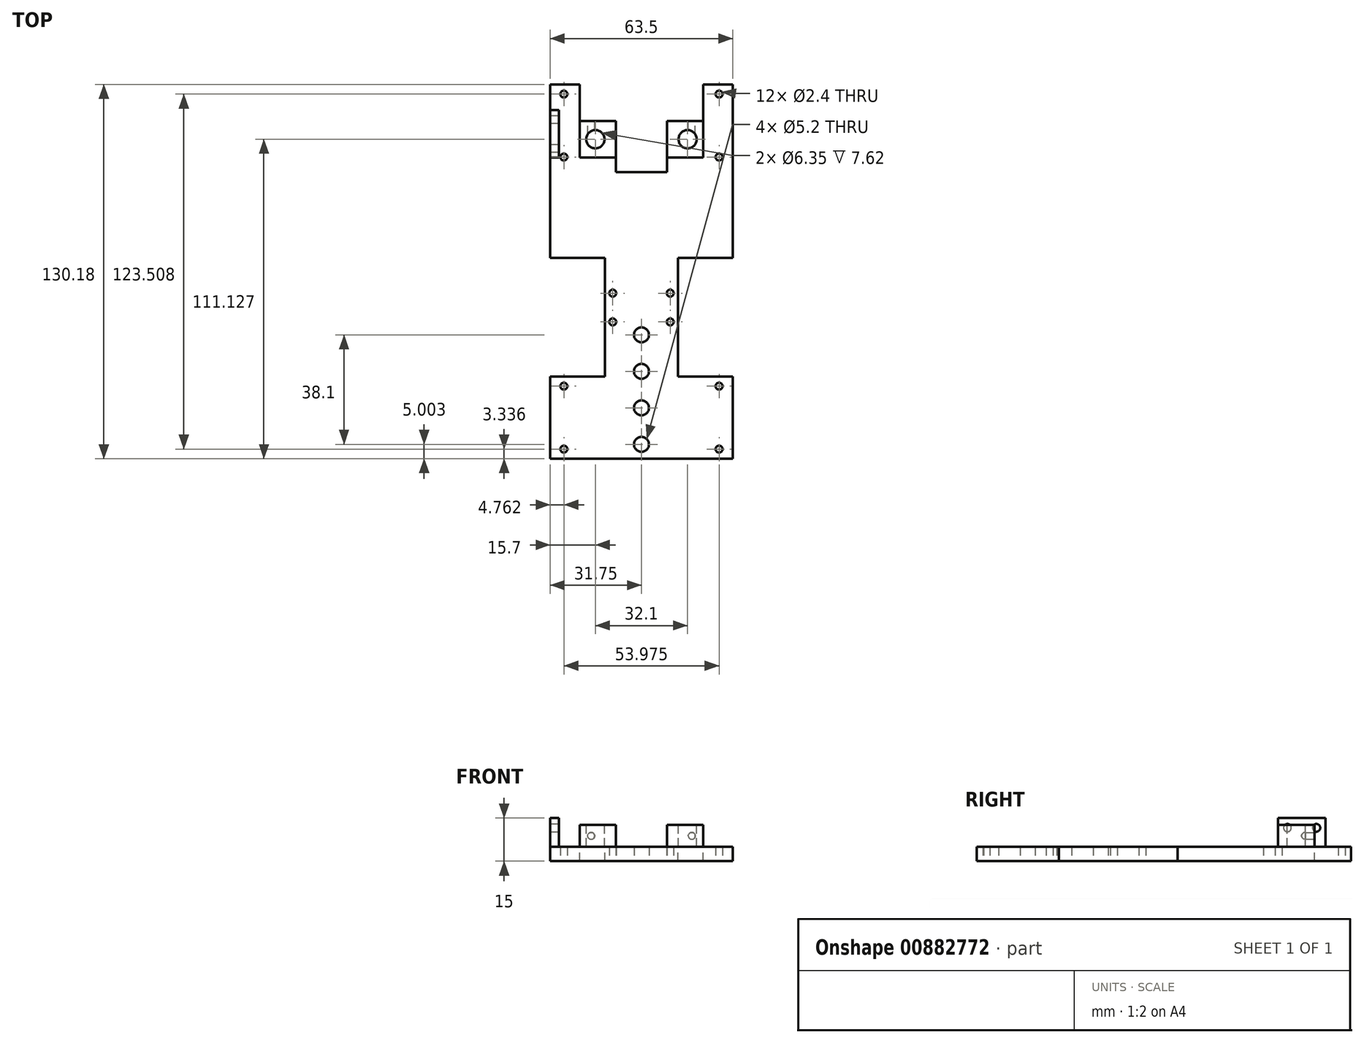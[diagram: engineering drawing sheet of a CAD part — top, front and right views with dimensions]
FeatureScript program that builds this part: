
annotation { "Feature Type Name" : "Feature", "Feature Type Description" : "" }
export const myFeature = defineFeature(function(context is Context, id is Id, definition is map)
    precondition{}
    {
        {
            var Q0;
            Q0=qCreatedBy(makeId("Top.planeOp"),FACE);
            var sketch = newSketch(context, id + "F0", { "sketchPlane" : qUnion([Q0])});
            skLineSegment(sketch, "E0.left", {"start": v(-12.7, 36.51) * mm, "end": v(-12.7, -36.51) * mm});
            skLineSegment(sketch, "E0.right", {"start": v(12.7, 36.51) * mm, "end": v(12.7, -36.51) * mm});
            skPoint(sketch, "E0.middle", {"position": v(0, 0) * mm});
            skLineSegment(sketch, "E1.bottom", {"start": v(-31.75, 65.09) * mm, "end": v(31.75, 65.09) * mm});
            skLineSegment(sketch, "E1.top", {"start": v(-31.75, 36.51) * mm, "end": v(-12.7, 36.51) * mm});
            skLineSegment(sketch, "E1.left", {"start": v(-31.75, 65.09) * mm, "end": v(-31.75, 36.51) * mm});
            skLineSegment(sketch, "E1.right", {"start": v(31.75, 65.09) * mm, "end": v(31.75, 36.51) * mm});
            skLineSegment(sketch, "E2.bottom", {"start": v(-31.75, -65.09) * mm, "end": v(31.75, -65.09) * mm});
            skLineSegment(sketch, "E2.top", {"start": v(-31.75, -36.51) * mm, "end": v(-12.7, -36.51) * mm});
            skLineSegment(sketch, "E2.left", {"start": v(-31.75, -65.09) * mm, "end": v(-31.75, -36.51) * mm});
            skLineSegment(sketch, "E2.right", {"start": v(31.75, -65.09) * mm, "end": v(31.75, -36.51) * mm});
            skLineSegment(sketch, "E3.trimOffspring", {"start": v(12.7, 36.51) * mm, "end": v(31.75, 36.51) * mm});
            skLineSegment(sketch, "E4.trimOffspring", {"start": v(12.7, -36.51) * mm, "end": v(31.75, -36.51) * mm});
            skLineSegment(sketch, "E5", {"start": v(0, -33.1) * mm, "end": v(0, -96.6) * mm});
            skLineSegment(sketch, "E6", {"start": v(-134.87, 0) * mm, "end": v(102.97, 0) * mm});
            skCircle(sketch, "E7", {"center": v(-26.99, 61.75) * mm, "radius": 1.2 * mm});
            skCircle(sketch, "E8", {"center": v(-26.99, 39.85) * mm, "radius": 1.2 * mm});
            skCircle(sketch, "E9", {"center": v(26.99, 61.75) * mm, "radius": 1.2 * mm});
            skCircle(sketch, "E10", {"center": v(26.99, 39.85) * mm, "radius": 1.2 * mm});
            skCircle(sketch, "E11", {"center": v(26.99, -39.85) * mm, "radius": 1.2 * mm});
            skCircle(sketch, "E12", {"center": v(26.99, -61.75) * mm, "radius": 1.2 * mm});
            skCircle(sketch, "E13", {"center": v(-26.99, -61.75) * mm, "radius": 1.2 * mm});
            skCircle(sketch, "E14", {"center": v(-26.99, -39.85) * mm, "radius": 1.2 * mm});
            skLineSegment(sketch, "E15", {"start": v(-31.75, 50.8) * mm, "end": v(31.75, 50.8) * mm});
            skLineSegment(sketch, "E16", {"start": v(-31.75, -50.8) * mm, "end": v(31.75, -50.8) * mm});
            skLineSegment(sketch, "E17.direction1", {"start": v(0, 60.09) * mm, "end": v(25.4, 60.09) * mm, "construction": true});
            skLineSegment(sketch, "E17.direction2", {"start": v(0, 60.09) * mm, "end": v(0, 47.39) * mm, "construction": true});
            skCircle(sketch, "E18", {"center": v(0, -60.09) * mm, "radius": 2.6 * mm});
            skCircle(sketch, "E19.0.1.0", {"center": v(0, -47.39) * mm, "radius": 2.6 * mm});
            skCircle(sketch, "E19.0.2.0", {"center": v(0, -34.69) * mm, "radius": 2.6 * mm});
            skCircle(sketch, "E19.0.3.0", {"center": v(0, -21.99) * mm, "radius": 2.6 * mm});
            skLineSegment(sketch, "E19.direction1", {"start": v(0, -60.09) * mm, "end": v(25.4, -60.09) * mm, "construction": true});
            skLineSegment(sketch, "E19.direction2", {"start": v(0, -60.09) * mm, "end": v(0, -47.39) * mm, "construction": true});
            skLineSegment(sketch, "E20", {"start": v(0, 65.09) * mm, "end": v(0, -50.8) * mm});
            skCircle(sketch, "E21", {"center": v(-10, -7.5) * mm, "radius": 1.2 * mm});
            skCircle(sketch, "E22", {"center": v(-10, -17.5) * mm, "radius": 1.2 * mm});
            skCircle(sketch, "E23.MirrorC", {"center": v(10, -7.5) * mm, "radius": 1.2 * mm});
            skCircle(sketch, "E24.MirrorC", {"center": v(10, -17.5) * mm, "radius": 1.2 * mm});
            skSolve(sketch);
        }
        {
            var Q0;
            Q0 = qSketchRegion(id + "F0", true);
            extrude(context, id + "F1", {"entities" : qUnion([Q0]), "depth" : 5 * mm, "offsetDistance" : 25.4 * mm});
        }
        {
            var Q0;
            Q0=makeQuery(id+"F1.opExtrude","CAP_FACE",FACE,{"disambiguationData":[OSD([sQuery(id+"F0.wireOp",EDGE,"E0.left"),sQuery(id+"F0.wireOp",EDGE,"E0.right"),sQuery(id+"F0.wireOp",EDGE,"E1.bottom"),sQuery(id+"F0.wireOp",EDGE,"E1.top"),sQuery(id+"F0.wireOp",EDGE,"E1.left"),sQuery(id+"F0.wireOp",EDGE,"E1.right"),sQuery(id+"F0.wireOp",EDGE,"E2.bottom"),sQuery(id+"F0.wireOp",EDGE,"E2.top"),sQuery(id+"F0.wireOp",EDGE,"E2.left"),sQuery(id+"F0.wireOp",EDGE,"E2.right"),sQuery(id+"F0.wireOp",EDGE,"E3.trimOffspring"),sQuery(id+"F0.wireOp",EDGE,"E4.trimOffspring"),sQuery(id+"F0.wireOp",EDGE,"E7"),sQuery(id+"F0.wireOp",EDGE,"E8"),sQuery(id+"F0.wireOp",EDGE,"E9"),sQuery(id+"F0.wireOp",EDGE,"E10"),sQuery(id+"F0.wireOp",EDGE,"E11"),sQuery(id+"F0.wireOp",EDGE,"E12"),sQuery(id+"F0.wireOp",EDGE,"E13"),sQuery(id+"F0.wireOp",EDGE,"E14"),sQuery(id+"F0.wireOp",EDGE,"E18"),sQuery(id+"F0.wireOp",EDGE,"E19.0.1.0"),sQuery(id+"F0.wireOp",EDGE,"E19.0.2.0"),sQuery(id+"F0.wireOp",EDGE,"E19.0.3.0"),sQuery(id+"F0.wireOp",EDGE,"E21"),sQuery(id+"F0.wireOp",EDGE,"E22"),sQuery(id+"F0.wireOp",EDGE,"E23.MirrorC"),sQuery(id+"F0.wireOp",EDGE,"E24.MirrorC")])],"isStart":false});
            var sketch = newSketch(context, id + "F2", { "sketchPlane" : qUnion([Q0])});
            skLineSegment(sketch, "E25.bottom", {"start": v(-31.75, 36.51) * mm, "end": v(-12.7, 36.51) * mm});
            skLineSegment(sketch, "E25.top", {"start": v(-31.75, 4.76) * mm, "end": v(-12.7, 4.76) * mm});
            skLineSegment(sketch, "E25.left", {"start": v(-31.75, 36.51) * mm, "end": v(-31.75, 4.76) * mm});
            skLineSegment(sketch, "E25.right", {"start": v(-12.7, 36.51) * mm, "end": v(-12.7, 4.76) * mm});
            skLineSegment(sketch, "E26.bottom", {"start": v(12.7, 36.51) * mm, "end": v(31.75, 36.51) * mm});
            skLineSegment(sketch, "E26.top", {"start": v(12.7, 4.76) * mm, "end": v(31.75, 4.76) * mm});
            skLineSegment(sketch, "E26.left", {"start": v(12.7, 36.51) * mm, "end": v(12.7, 4.76) * mm});
            skLineSegment(sketch, "E26.right", {"start": v(31.75, 36.51) * mm, "end": v(31.75, 4.76) * mm});
            skSolve(sketch);
        }
        {
            var Q0;
            Q0 = qSketchRegion(id + "F2", true);
            var Q1;
            Q1=makeQuery(id+"F1.opExtrude","CAP_FACE",FACE,{"disambiguationData":[OSD([sQuery(id+"F0.wireOp",EDGE,"E0.left"),sQuery(id+"F0.wireOp",EDGE,"E0.right"),sQuery(id+"F0.wireOp",EDGE,"E1.bottom"),sQuery(id+"F0.wireOp",EDGE,"E1.top"),sQuery(id+"F0.wireOp",EDGE,"E1.left"),sQuery(id+"F0.wireOp",EDGE,"E1.right"),sQuery(id+"F0.wireOp",EDGE,"E2.bottom"),sQuery(id+"F0.wireOp",EDGE,"E2.top"),sQuery(id+"F0.wireOp",EDGE,"E2.left"),sQuery(id+"F0.wireOp",EDGE,"E2.right"),sQuery(id+"F0.wireOp",EDGE,"E3.trimOffspring"),sQuery(id+"F0.wireOp",EDGE,"E4.trimOffspring"),sQuery(id+"F0.wireOp",EDGE,"E7"),sQuery(id+"F0.wireOp",EDGE,"E8"),sQuery(id+"F0.wireOp",EDGE,"E9"),sQuery(id+"F0.wireOp",EDGE,"E10"),sQuery(id+"F0.wireOp",EDGE,"E11"),sQuery(id+"F0.wireOp",EDGE,"E12"),sQuery(id+"F0.wireOp",EDGE,"E13"),sQuery(id+"F0.wireOp",EDGE,"E14"),sQuery(id+"F0.wireOp",EDGE,"E18"),sQuery(id+"F0.wireOp",EDGE,"E19.0.1.0"),sQuery(id+"F0.wireOp",EDGE,"E19.0.2.0"),sQuery(id+"F0.wireOp",EDGE,"E19.0.3.0"),sQuery(id+"F0.wireOp",EDGE,"E21"),sQuery(id+"F0.wireOp",EDGE,"E22"),sQuery(id+"F0.wireOp",EDGE,"E23.MirrorC"),sQuery(id+"F0.wireOp",EDGE,"E24.MirrorC")])],"isStart":true});
            extrude(context, id + "F3", {"entities" : qUnion([Q0]), "operationType" : NewBodyOperationType.ADD, "endBound" : BoundingType.UP_TO_SURFACE, "oppositeDirection" : true, "depth" : 25.4 * mm, "endBoundEntityFace" : qUnion([Q1]), "offsetDistance" : 25.4 * mm});
        }
        {
            var Q0;
            Q0=makeQuery(id+"F3.boolean.opBoolean","MERGE",FACE,{"derivedFrom":[makeQuery(id+"F1.opExtrude","CAP_FACE",FACE,{"disambiguationData":[OSD([sQuery(id+"F0.wireOp",EDGE,"E0.left"),sQuery(id+"F0.wireOp",EDGE,"E0.right"),sQuery(id+"F0.wireOp",EDGE,"E1.bottom"),sQuery(id+"F0.wireOp",EDGE,"E1.top"),sQuery(id+"F0.wireOp",EDGE,"E1.left"),sQuery(id+"F0.wireOp",EDGE,"E1.right"),sQuery(id+"F0.wireOp",EDGE,"E2.bottom"),sQuery(id+"F0.wireOp",EDGE,"E2.top"),sQuery(id+"F0.wireOp",EDGE,"E2.left"),sQuery(id+"F0.wireOp",EDGE,"E2.right"),sQuery(id+"F0.wireOp",EDGE,"E3.trimOffspring"),sQuery(id+"F0.wireOp",EDGE,"E4.trimOffspring"),sQuery(id+"F0.wireOp",EDGE,"E7"),sQuery(id+"F0.wireOp",EDGE,"E8"),sQuery(id+"F0.wireOp",EDGE,"E9"),sQuery(id+"F0.wireOp",EDGE,"E10"),sQuery(id+"F0.wireOp",EDGE,"E11"),sQuery(id+"F0.wireOp",EDGE,"E12"),sQuery(id+"F0.wireOp",EDGE,"E13"),sQuery(id+"F0.wireOp",EDGE,"E14"),sQuery(id+"F0.wireOp",EDGE,"E18"),sQuery(id+"F0.wireOp",EDGE,"E19.0.1.0"),sQuery(id+"F0.wireOp",EDGE,"E19.0.2.0"),sQuery(id+"F0.wireOp",EDGE,"E19.0.3.0"),sQuery(id+"F0.wireOp",EDGE,"E21"),sQuery(id+"F0.wireOp",EDGE,"E22"),sQuery(id+"F0.wireOp",EDGE,"E23.MirrorC"),sQuery(id+"F0.wireOp",EDGE,"E24.MirrorC")])],"isStart":false}),makeQuery(id+"F3.opExtrude","CAP_FACE",FACE,{"disambiguationData":[OSD([sQuery(id+"F2.wireOp",EDGE,"E25.bottom"),sQuery(id+"F2.wireOp",EDGE,"E25.top"),sQuery(id+"F2.wireOp",EDGE,"E25.left"),sQuery(id+"F2.wireOp",EDGE,"E25.right")])],"isStart":true}),makeQuery(id+"F3.opExtrude","CAP_FACE",FACE,{"disambiguationData":[OSD([sQuery(id+"F2.wireOp",EDGE,"E26.bottom"),sQuery(id+"F2.wireOp",EDGE,"E26.top"),sQuery(id+"F2.wireOp",EDGE,"E26.left"),sQuery(id+"F2.wireOp",EDGE,"E26.right")])],"isStart":true})]});
            var sketch = newSketch(context, id + "F4", { "sketchPlane" : qUnion([Q0])});
            skLineSegment(sketch, "E27.bottom", {"start": v(-21.5, 65.09) * mm, "end": v(21.5, 65.09) * mm});
            skLineSegment(sketch, "E27.top", {"start": v(-21.5, 52.39) * mm, "end": v(21.5, 52.39) * mm});
            skLineSegment(sketch, "E27.left", {"start": v(-21.5, 65.09) * mm, "end": v(-21.5, 52.39) * mm});
            skLineSegment(sketch, "E27.right", {"start": v(21.5, 65.09) * mm, "end": v(21.5, 52.39) * mm});
            skSolve(sketch);
        }
        {
            var Q0;
            Q0 = qSketchRegion(id + "F4", true);
            extrude(context, id + "F5", {"entities" : qUnion([Q0]), "operationType" : NewBodyOperationType.REMOVE, "endBound" : BoundingType.UP_TO_NEXT, "oppositeDirection" : true, "depth" : 25.4 * mm, "offsetDistance" : 25.4 * mm});
        }
        {
            var Q0;
            Q0=makeQuery(id+"F3.boolean.opBoolean","MERGE",FACE,{"derivedFrom":[makeQuery(id+"F1.opExtrude","CAP_FACE",FACE,{"disambiguationData":[OSD([sQuery(id+"F0.wireOp",EDGE,"E0.left"),sQuery(id+"F0.wireOp",EDGE,"E0.right"),sQuery(id+"F0.wireOp",EDGE,"E1.bottom"),sQuery(id+"F0.wireOp",EDGE,"E1.top"),sQuery(id+"F0.wireOp",EDGE,"E1.left"),sQuery(id+"F0.wireOp",EDGE,"E1.right"),sQuery(id+"F0.wireOp",EDGE,"E2.bottom"),sQuery(id+"F0.wireOp",EDGE,"E2.top"),sQuery(id+"F0.wireOp",EDGE,"E2.left"),sQuery(id+"F0.wireOp",EDGE,"E2.right"),sQuery(id+"F0.wireOp",EDGE,"E3.trimOffspring"),sQuery(id+"F0.wireOp",EDGE,"E4.trimOffspring"),sQuery(id+"F0.wireOp",EDGE,"E7"),sQuery(id+"F0.wireOp",EDGE,"E8"),sQuery(id+"F0.wireOp",EDGE,"E9"),sQuery(id+"F0.wireOp",EDGE,"E10"),sQuery(id+"F0.wireOp",EDGE,"E11"),sQuery(id+"F0.wireOp",EDGE,"E12"),sQuery(id+"F0.wireOp",EDGE,"E13"),sQuery(id+"F0.wireOp",EDGE,"E14"),sQuery(id+"F0.wireOp",EDGE,"E18"),sQuery(id+"F0.wireOp",EDGE,"E19.0.1.0"),sQuery(id+"F0.wireOp",EDGE,"E19.0.2.0"),sQuery(id+"F0.wireOp",EDGE,"E19.0.3.0"),sQuery(id+"F0.wireOp",EDGE,"E21"),sQuery(id+"F0.wireOp",EDGE,"E22"),sQuery(id+"F0.wireOp",EDGE,"E23.MirrorC"),sQuery(id+"F0.wireOp",EDGE,"E24.MirrorC")])],"isStart":true}),makeQuery(id+"F3.opExtrude","CAP_FACE",FACE,{"disambiguationData":[OSD([sQuery(id+"F2.wireOp",EDGE,"E25.bottom"),sQuery(id+"F2.wireOp",EDGE,"E25.top"),sQuery(id+"F2.wireOp",EDGE,"E25.left"),sQuery(id+"F2.wireOp",EDGE,"E25.right")])],"isStart":false}),makeQuery(id+"F3.opExtrude","CAP_FACE",FACE,{"disambiguationData":[OSD([sQuery(id+"F2.wireOp",EDGE,"E26.bottom"),sQuery(id+"F2.wireOp",EDGE,"E26.top"),sQuery(id+"F2.wireOp",EDGE,"E26.left"),sQuery(id+"F2.wireOp",EDGE,"E26.right")])],"isStart":false})]});
            var sketch = newSketch(context, id + "F6", { "sketchPlane" : qUnion([Q0])});
            skLineSegment(sketch, "E28.bottom", {"start": v(-8.9, -34.6) * mm, "end": v(8.9, -34.6) * mm});
            skLineSegment(sketch, "E28.top", {"start": v(-8.9, -52.39) * mm, "end": v(8.9, -52.39) * mm});
            skLineSegment(sketch, "E28.left", {"start": v(-8.9, -34.6) * mm, "end": v(-8.9, -52.39) * mm});
            skLineSegment(sketch, "E28.right", {"start": v(8.89, -34.6) * mm, "end": v(8.89, -52.39) * mm});
            skSolve(sketch);
        }
        {
            var Q0;
            Q0 = qSketchRegion(id + "F6", true);
            extrude(context, id + "F7", {"entities" : qUnion([Q0]), "operationType" : NewBodyOperationType.REMOVE, "endBound" : BoundingType.UP_TO_NEXT, "oppositeDirection" : true, "depth" : 25.4 * mm, "offsetDistance" : 25.4 * mm});
        }
        {
            var Q0;
            Q0=makeQuery(id+"F3.boolean.opBoolean","MERGE",FACE,{"derivedFrom":[makeQuery(id+"F1.opExtrude","CAP_FACE",FACE,{"disambiguationData":[OSD([sQuery(id+"F0.wireOp",EDGE,"E0.left"),sQuery(id+"F0.wireOp",EDGE,"E0.right"),sQuery(id+"F0.wireOp",EDGE,"E1.bottom"),sQuery(id+"F0.wireOp",EDGE,"E1.top"),sQuery(id+"F0.wireOp",EDGE,"E1.left"),sQuery(id+"F0.wireOp",EDGE,"E1.right"),sQuery(id+"F0.wireOp",EDGE,"E2.bottom"),sQuery(id+"F0.wireOp",EDGE,"E2.top"),sQuery(id+"F0.wireOp",EDGE,"E2.left"),sQuery(id+"F0.wireOp",EDGE,"E2.right"),sQuery(id+"F0.wireOp",EDGE,"E3.trimOffspring"),sQuery(id+"F0.wireOp",EDGE,"E4.trimOffspring"),sQuery(id+"F0.wireOp",EDGE,"E7"),sQuery(id+"F0.wireOp",EDGE,"E8"),sQuery(id+"F0.wireOp",EDGE,"E9"),sQuery(id+"F0.wireOp",EDGE,"E10"),sQuery(id+"F0.wireOp",EDGE,"E11"),sQuery(id+"F0.wireOp",EDGE,"E12"),sQuery(id+"F0.wireOp",EDGE,"E13"),sQuery(id+"F0.wireOp",EDGE,"E14"),sQuery(id+"F0.wireOp",EDGE,"E18"),sQuery(id+"F0.wireOp",EDGE,"E19.0.1.0"),sQuery(id+"F0.wireOp",EDGE,"E19.0.2.0"),sQuery(id+"F0.wireOp",EDGE,"E19.0.3.0"),sQuery(id+"F0.wireOp",EDGE,"E21"),sQuery(id+"F0.wireOp",EDGE,"E22"),sQuery(id+"F0.wireOp",EDGE,"E23.MirrorC"),sQuery(id+"F0.wireOp",EDGE,"E24.MirrorC")])],"isStart":false}),makeQuery(id+"F3.opExtrude","CAP_FACE",FACE,{"disambiguationData":[OSD([sQuery(id+"F2.wireOp",EDGE,"E25.bottom"),sQuery(id+"F2.wireOp",EDGE,"E25.top"),sQuery(id+"F2.wireOp",EDGE,"E25.left"),sQuery(id+"F2.wireOp",EDGE,"E25.right")])],"isStart":true}),makeQuery(id+"F3.opExtrude","CAP_FACE",FACE,{"disambiguationData":[OSD([sQuery(id+"F2.wireOp",EDGE,"E26.bottom"),sQuery(id+"F2.wireOp",EDGE,"E26.top"),sQuery(id+"F2.wireOp",EDGE,"E26.left"),sQuery(id+"F2.wireOp",EDGE,"E26.right")])],"isStart":true})]});
            var sketch = newSketch(context, id + "F8", { "sketchPlane" : qUnion([Q0])});
            skLineSegment(sketch, "E29.bottom", {"start": v(-8.9, 52.39) * mm, "end": v(-21.5, 52.39) * mm});
            skLineSegment(sketch, "E29.top", {"start": v(-8.89, 39.69) * mm, "end": v(-21.5, 39.69) * mm});
            skLineSegment(sketch, "E29.left", {"start": v(-8.9, 52.39) * mm, "end": v(-8.9, 39.69) * mm});
            skLineSegment(sketch, "E29.right", {"start": v(-21.5, 52.39) * mm, "end": v(-21.5, 39.69) * mm});
            skLineSegment(sketch, "E30.MirrorCS", {"start": v(8.89, 39.69) * mm, "end": v(21.5, 39.69) * mm});
            skLineSegment(sketch, "E31.MirrorCS", {"start": v(8.9, 52.39) * mm, "end": v(8.9, 39.69) * mm});
            skLineSegment(sketch, "E32.MirrorCS", {"start": v(8.9, 52.39) * mm, "end": v(21.5, 52.39) * mm});
            skLineSegment(sketch, "E33.MirrorCS", {"start": v(21.5, 52.39) * mm, "end": v(21.5, 39.69) * mm});
            skSolve(sketch);
        }
        {
            var Q0;
            Q0 = qSketchRegion(id + "F8", true);
            extrude(context, id + "F9", {"entities" : qUnion([Q0]), "operationType" : NewBodyOperationType.ADD, "depth" : 7.62 * mm, "offsetDistance" : 25.4 * mm});
        }
        {
            var Q0;
            Q0=makeQuery(id+"F9.opExtrude","CAP_FACE",FACE,{"disambiguationData":[OSD([sQuery(id+"F8.wireOp",EDGE,"E29.bottom"),sQuery(id+"F8.wireOp",EDGE,"E29.top"),sQuery(id+"F8.wireOp",EDGE,"E29.left"),sQuery(id+"F8.wireOp",EDGE,"E29.right")])],"isStart":false});
            var sketch = newSketch(context, id + "F10", { "sketchPlane" : qUnion([Q0])});
            skCircle(sketch, "E34", {"center": v(-16.05, 46.04) * mm, "radius": 3.18 * mm});
            skCircle(sketch, "E35.MirrorC", {"center": v(16.05, 46.04) * mm, "radius": 3.18 * mm});
            skLineSegment(sketch, "E36", {"start": v(-21.5, 46.04) * mm, "end": v(-8.9, 46.04) * mm});
            skSolve(sketch);
        }
        {
            var Q0;
            Q0 = qSketchRegion(id + "F10", true);
            extrude(context, id + "F11", {"entities" : qUnion([Q0]), "operationType" : NewBodyOperationType.REMOVE, "oppositeDirection" : true, "depth" : 7.62 * mm, "offsetDistance" : 25.4 * mm});
        }
        {
            var Q0;
            Q0=makeQuery(id+"F9.boolean.opBoolean","MERGE",FACE,{"derivedFrom":[makeQuery(id+"F7.boolean.opBoolean","SPLIT",FACE,{"disambiguationData":[TD([makeQuery(id+"F5.boolean.opBoolean","COPY",FACE,{"derivedFrom":makeQuery(id+"F5.opExtrude","SWEPT_FACE",FACE,{"disambiguationData":[OSD([sQuery(id+"F4.wireOp",EDGE,"E27.left")])]})})])],"derivedFrom":makeQuery(id+"F5.boolean.opBoolean","COPY",FACE,{"derivedFrom":makeQuery(id+"F5.opExtrude","SWEPT_FACE",FACE,{"disambiguationData":[OSD([sQuery(id+"F4.wireOp",EDGE,"E27.top")])]})})}),makeQuery(id+"F9.opExtrude","SWEPT_FACE",FACE,{"disambiguationData":[OSD([sQuery(id+"F8.wireOp",EDGE,"E29.bottom")])]})]});
            var sketch = newSketch(context, id + "F12", { "sketchPlane" : qUnion([Q0])});
            skCircle(sketch, "E37", {"center": v(17.5, 8.8) * mm, "radius": 1.2 * mm});
            skCircle(sketch, "E38.MirrorC", {"center": v(-17.5, 8.8) * mm, "radius": 1.2 * mm});
            skSolve(sketch);
        }
        {
            var Q0;
            Q0 = qSketchRegion(id + "F12", true);
            extrude(context, id + "F13", {"entities" : qUnion([Q0]), "operationType" : NewBodyOperationType.REMOVE, "oppositeDirection" : true, "depth" : 6 * mm, "offsetDistance" : 25.4 * mm});
        }
        {
            var Q0;
            Q0=makeQuery(id+"F3.boolean.opBoolean","MERGE",FACE,{"derivedFrom":[makeQuery(id+"F1.opExtrude","CAP_FACE",FACE,{"disambiguationData":[OSD([sQuery(id+"F0.wireOp",EDGE,"E0.left"),sQuery(id+"F0.wireOp",EDGE,"E0.right"),sQuery(id+"F0.wireOp",EDGE,"E1.bottom"),sQuery(id+"F0.wireOp",EDGE,"E1.top"),sQuery(id+"F0.wireOp",EDGE,"E1.left"),sQuery(id+"F0.wireOp",EDGE,"E1.right"),sQuery(id+"F0.wireOp",EDGE,"E2.bottom"),sQuery(id+"F0.wireOp",EDGE,"E2.top"),sQuery(id+"F0.wireOp",EDGE,"E2.left"),sQuery(id+"F0.wireOp",EDGE,"E2.right"),sQuery(id+"F0.wireOp",EDGE,"E3.trimOffspring"),sQuery(id+"F0.wireOp",EDGE,"E4.trimOffspring"),sQuery(id+"F0.wireOp",EDGE,"E7"),sQuery(id+"F0.wireOp",EDGE,"E8"),sQuery(id+"F0.wireOp",EDGE,"E9"),sQuery(id+"F0.wireOp",EDGE,"E10"),sQuery(id+"F0.wireOp",EDGE,"E11"),sQuery(id+"F0.wireOp",EDGE,"E12"),sQuery(id+"F0.wireOp",EDGE,"E13"),sQuery(id+"F0.wireOp",EDGE,"E14"),sQuery(id+"F0.wireOp",EDGE,"E18"),sQuery(id+"F0.wireOp",EDGE,"E19.0.1.0"),sQuery(id+"F0.wireOp",EDGE,"E19.0.2.0"),sQuery(id+"F0.wireOp",EDGE,"E19.0.3.0"),sQuery(id+"F0.wireOp",EDGE,"E21"),sQuery(id+"F0.wireOp",EDGE,"E22"),sQuery(id+"F0.wireOp",EDGE,"E23.MirrorC"),sQuery(id+"F0.wireOp",EDGE,"E24.MirrorC")])],"isStart":false}),makeQuery(id+"F3.opExtrude","CAP_FACE",FACE,{"disambiguationData":[OSD([sQuery(id+"F2.wireOp",EDGE,"E25.bottom"),sQuery(id+"F2.wireOp",EDGE,"E25.top"),sQuery(id+"F2.wireOp",EDGE,"E25.left"),sQuery(id+"F2.wireOp",EDGE,"E25.right")])],"isStart":true}),makeQuery(id+"F3.opExtrude","CAP_FACE",FACE,{"disambiguationData":[OSD([sQuery(id+"F2.wireOp",EDGE,"E26.bottom"),sQuery(id+"F2.wireOp",EDGE,"E26.top"),sQuery(id+"F2.wireOp",EDGE,"E26.left"),sQuery(id+"F2.wireOp",EDGE,"E26.right")])],"isStart":true})]});
            var sketch = newSketch(context, id + "F14", { "sketchPlane" : qUnion([Q0])});
            skLineSegment(sketch, "E39.bottom", {"start": v(-31.75, 56.2) * mm, "end": v(-28.75, 56.2) * mm});
            skLineSegment(sketch, "E39.top", {"start": v(-31.75, 39.69) * mm, "end": v(-28.75, 39.69) * mm});
            skLineSegment(sketch, "E39.left", {"start": v(-31.75, 56.2) * mm, "end": v(-31.75, 39.69) * mm});
            skLineSegment(sketch, "E39.right", {"start": v(-28.75, 56.2) * mm, "end": v(-28.75, 39.69) * mm});
            skSolve(sketch);
        }
        {
            var Q0;
            Q0 = qSketchRegion(id + "F14", true);
            extrude(context, id + "F15", {"entities" : qUnion([Q0]), "operationType" : NewBodyOperationType.ADD, "depth" : 10 * mm, "offsetDistance" : 25.4 * mm});
        }
        {
            var Q0;
            Q0=makeQuery(id+"F15.opExtrude","SWEPT_FACE",FACE,{"disambiguationData":[OSD([sQuery(id+"F14.wireOp",EDGE,"E39.right")])]});
            var sketch = newSketch(context, id + "F16", { "sketchPlane" : qUnion([Q0])});
            skCircle(sketch, "E40", {"center": v(42.92, 11.6) * mm, "radius": 1.35 * mm});
            skCircle(sketch, "E41", {"center": v(52.97, 11.6) * mm, "radius": 1.35 * mm});
            skLineSegment(sketch, "E42", {"start": v(47.94, 15) * mm, "end": v(47.94, 5) * mm});
            skSolve(sketch);
        }
        {
            var Q0;
            Q0 = qSketchRegion(id + "F16", true);
            extrude(context, id + "F17", {"entities" : qUnion([Q0]), "operationType" : NewBodyOperationType.REMOVE, "endBound" : BoundingType.UP_TO_NEXT, "oppositeDirection" : true, "depth" : 25.4 * mm, "offsetDistance" : 25.4 * mm});
        }
    });
